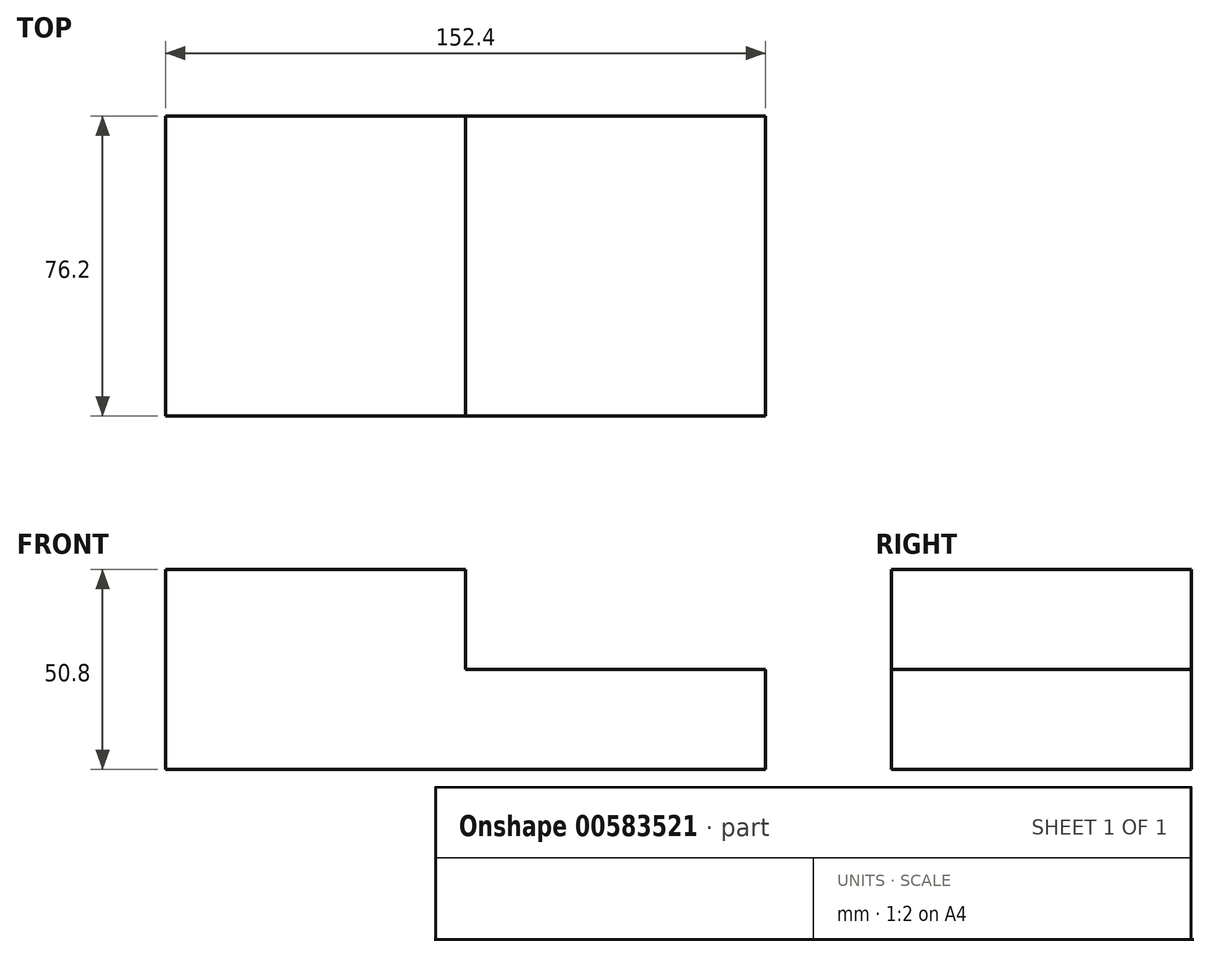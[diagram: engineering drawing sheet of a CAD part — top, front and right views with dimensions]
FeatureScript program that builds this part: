
annotation { "Feature Type Name" : "Feature", "Feature Type Description" : "" }
export const myFeature = defineFeature(function(context is Context, id is Id, definition is map)
    precondition{}
    {
        {
            var Q0;
            Q0=qCreatedBy(makeId("Front.planeOp"),FACE);
            var sketch = newSketch(context, id + "F0", { "sketchPlane" : qUnion([Q0])});
            skLineSegment(sketch, "E0", {"start": v(0, 0) * mm, "end": v(152.4, 0) * mm});
            skLineSegment(sketch, "E1", {"start": v(0, 0) * mm, "end": v(0, 50.8) * mm});
            skLineSegment(sketch, "E2", {"start": v(0, 50.8) * mm, "end": v(76.2, 50.8) * mm});
            skLineSegment(sketch, "E3", {"start": v(76.2, 50.8) * mm, "end": v(76.2, 25.4) * mm});
            skLineSegment(sketch, "E4", {"start": v(76.2, 25.4) * mm, "end": v(152.4, 25.4) * mm});
            skLineSegment(sketch, "E5", {"start": v(152.4, 25.4) * mm, "end": v(152.4, 0) * mm});
            skSolve(sketch);
        }
        {
            var Q0;
            Q0 = qSketchRegion(id + "F0", true);
            extrude(context, id + "F1", {"entities" : qUnion([Q0]), "depth" : 76.2 * mm, "offsetDistance" : 25.4 * mm});
        }
    });
